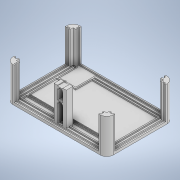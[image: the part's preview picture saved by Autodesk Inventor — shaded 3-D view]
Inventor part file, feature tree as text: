
AUTODESK INVENTOR PART (.ipt)
format: ipt  version: 2021 (Build 250183000, 183)  size: 399,872 bytes
history: native  units: mm
features: extrude x9, sketch x6, projected_geometry x5
ambient origin geometry x8: Origin, YZ Plane, XZ Plane, XY Plane, X Axis, Y Axis, Z Axis, Center Point
bodies: Volumenkörper1 (feature_tree)
feature tree (20):
  extrude  "Extrusion1"  Depth=100.0mm
  sketch  "Skizze2"  dims[d2=10.0mm d3=2.0mm d4=0.0mm]
  extrude  "Extrusion2"  Depth=2.0mm TaperAngle=0.0deg
  extrude  "Extrusion3"  Depth=2.0mm
  extrude  "Extrusion4"  Depth=2.0mm
  sketch  "Skizze4"  dims[d7=2.0mm d12=2.0mm]
  extrude  "Extrusion5"  Depth=0.5mm
  extrude  "Extrusion6"  Depth=2.0mm TaperAngle=0.0deg
  extrude  "Extrusion9"  Depth=50.0mm TaperAngle=0.0deg
  extrude  "Extrusion7"  Depth=2.0mm
  extrude  "Extrusion8"  Depth=11.5mm
  sketch  "Skizze1"  dims[d0=150.0mm d1=100.0mm]
  projected_geometry  "Projizierte Kontur1"
  sketch  "Skizze3"  dims[d5=3.5mm d6=2.0mm]
  projected_geometry  "Projizierte Kontur2"
  projected_geometry  "Projizierte Kontur3"
  sketch  "Skizze5"  dims[d13=2.0mm d14=0.5mm]
  projected_geometry  "Projizierte Kontur4"
  sketch  "Skizze6"  dims[d15=2.0mm d16=2.0mm d17=0.0mm d18=50.0mm d19=0.0mm d20=2.0mm d21=11.5mm d22=1.0mm d23=1.0mm d24=10.0mm d25=0.0mm d26=1.0mm d27=26.0mm d28=29.0mm d29=0.0mm d30=0.0mm d31=2.0mm d32=2.0mm d33=2.0mm d34=0.0mm d41=10.0mm d42=8.0mm d43=5.0mm d44=49.0mm d45=2.0mm d46=0.0mm d47=0.0mm d48=5.0mm d49=5.0mm d50=1.0mm d51=13.0mm d52=50.0mm d53=0.0mm d54=1.9mm d55=4.0mm d56=5.0mm d57=0.0mm]
  projected_geometry  "Projizierte Kontur5"
